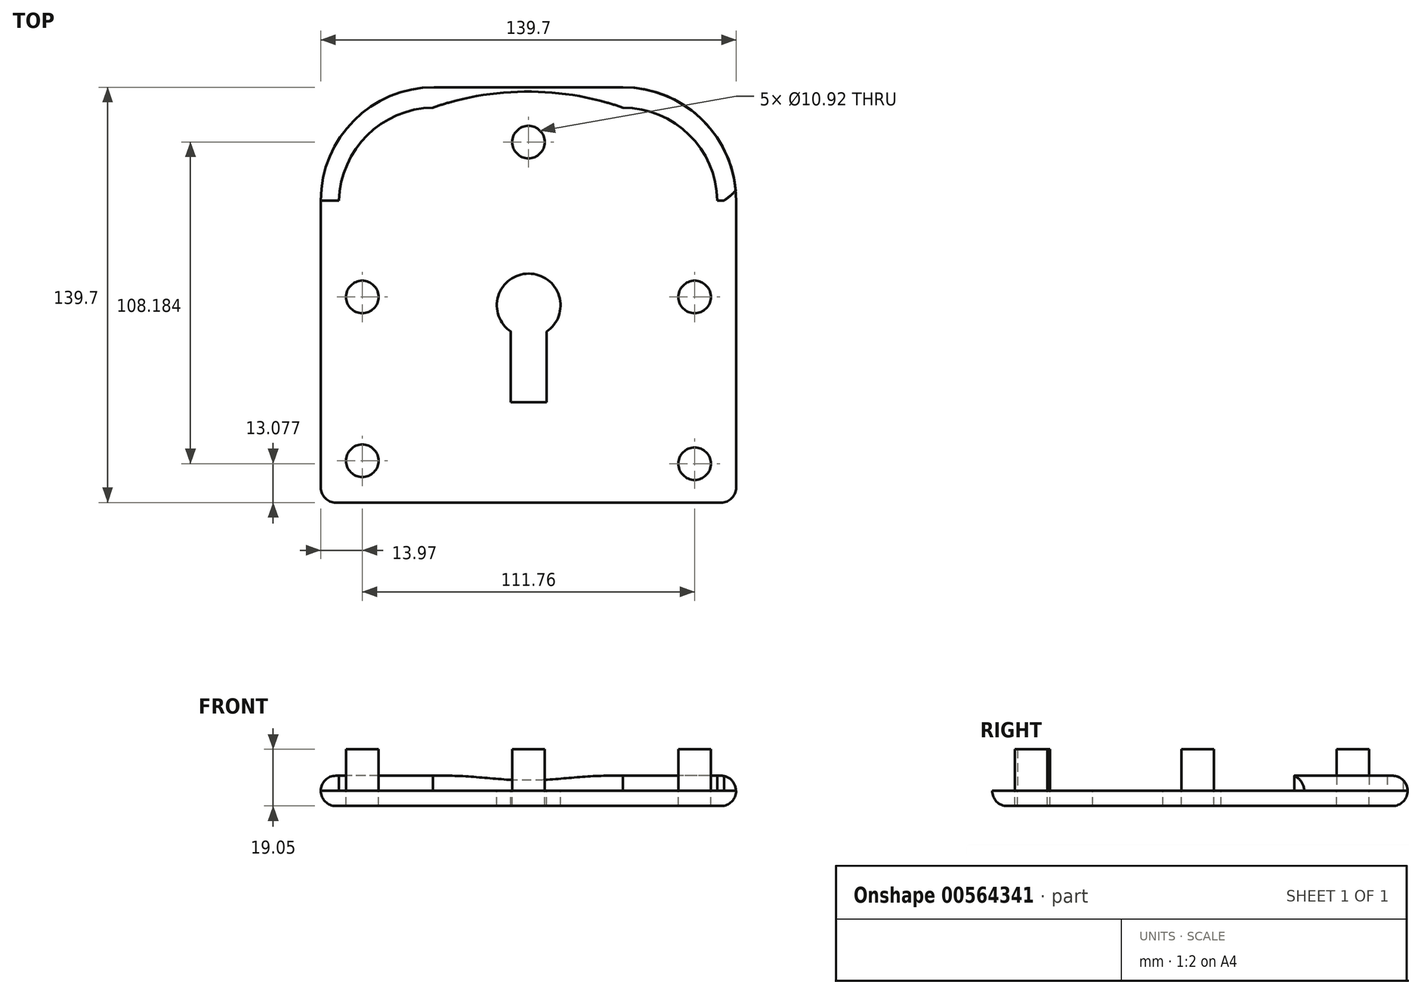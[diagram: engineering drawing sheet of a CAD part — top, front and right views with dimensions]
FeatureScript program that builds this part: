
annotation { "Feature Type Name" : "Feature", "Feature Type Description" : "" }
export const myFeature = defineFeature(function(context is Context, id is Id, definition is map)
    precondition{}
    {
        {
            var Q0;
            Q0=qCreatedBy(makeId("Top.planeOp"),FACE);
            var sketch = newSketch(context, id + "F0", { "sketchPlane" : qUnion([Q0])});
            skLineSegment(sketch, "E0.bottom", {"start": v(-31.75, 79.19) * mm, "end": v(31.75, 79.19) * mm});
            skLineSegment(sketch, "E0.top", {"start": v(-69.85, -60.51) * mm, "end": v(69.85, -60.51) * mm});
            skLineSegment(sketch, "E0.left", {"start": v(-69.85, 41.09) * mm, "end": v(-69.85, -60.51) * mm});
            skLineSegment(sketch, "E0.right", {"start": v(69.85, 41.09) * mm, "end": v(69.85, -60.51) * mm});
            skPoint(sketch, "E1.0.internal.snap0", {"position": v(0, -60.51) * mm});
            skPoint(sketch, "E2.orphan", {"position": v(-69.85, 32.63) * mm});
            skPoint(sketch, "E3.1.internal.snap0", {"position": v(27.83, 44.56) * mm});
            skFitSpline(sketch, "E3", {"points": [v(27.83, 44.56) * mm, v(69.85, 44.56) * mm], "startDerivative": vector(74.5, -35.49) * mm, "endDerivative": vector(22.58, 22.62) * mm});
            skPoint(sketch, "E4.orphan", {"position": v(73.2, 110.43) * mm});
            skPoint(sketch, "E5.start.orphan", {"position": v(69.85, 41.09) * mm});
            skCircle(sketch, "E6", {"center": v(0, 60.75) * mm, "radius": 5.46 * mm});
            skCircle(sketch, "E7", {"center": v(55.88, 8.65) * mm, "radius": 5.46 * mm});
            skCircle(sketch, "E8", {"center": v(55.88, -47.43) * mm, "radius": 5.46 * mm});
            skPoint(sketch, "E9.visualSharp", {"position": v(-69.85, 79.19) * mm});
            skArc(sketch, "E9.filletArc", {"start": v(-31.75, 79.19) * mm, "mid": v(-58.7, 68.03) * mm, "end": v(-69.85, 41.09) * mm});
            skPoint(sketch, "E10.visualSharp", {"position": v(69.85, 79.19) * mm});
            skArc(sketch, "E10.filletArc", {"start": v(69.85, 41.09) * mm, "mid": v(58.7, 68.03) * mm, "end": v(31.75, 79.19) * mm});
            skCircle(sketch, "E11", {"center": v(-55.88, 8.65) * mm, "radius": 5.46 * mm});
            skCircle(sketch, "E12", {"center": v(-55.88, -46.46) * mm, "radius": 5.46 * mm});
            skPoint(sketch, "E13.start.orphan", {"position": v(0, 79.19) * mm});
            skPoint(sketch, "E14.end.orphan", {"position": v(0, 74.72) * mm});
            skPoint(sketch, "E15.start.orphan", {"position": v(-64.1, 32.63) * mm});
            skPoint(sketch, "E16.end.orphan", {"position": v(-58.36, 32.63) * mm});
            skPoint(sketch, "E17.end.orphan", {"position": v(128.83, 32.86) * mm});
            skPoint(sketch, "E18.end.orphan", {"position": v(41.2, 32.63) * mm});
            skPoint(sketch, "E19.right.end.orphan", {"position": v(-17.52, -21.31) * mm});
            skPoint(sketch, "E20.left.start.orphan", {"position": v(48.52, 32.63) * mm});
            skPoint(sketch, "E21.top.end.orphan", {"position": v(10.9, -44.82) * mm});
            skPoint(sketch, "E22.start.orphan", {"position": v(0, -44.82) * mm});
            skPoint(sketch, "E23.bottom.start.orphan", {"position": v(44.9, 0) * mm});
            skPoint(sketch, "E24.bottom.start.orphan", {"position": v(-62.6, 0) * mm});
            skLineSegment(sketch, "E25", {"start": v(-69.85, 41.09) * mm, "end": v(-63.7, 41.09) * mm});
            skLineSegment(sketch, "E26.bottom", {"start": v(-5.9, -3.04) * mm, "end": v(-5.91, -3.04) * mm});
            skLineSegment(sketch, "E26.top", {"start": v(6.06, -26.7) * mm, "end": v(-5.91, -26.7) * mm});
            skLineSegment(sketch, "E26.left", {"start": v(6.06, -3.04) * mm, "end": v(6.06, -26.7) * mm});
            skLineSegment(sketch, "E26.right", {"start": v(-5.91, -3.04) * mm, "end": v(-5.91, -26.7) * mm});
            skArc(sketch, "E27", {"start": v(-32.19, 72.34) * mm, "mid": v(-54.23, 63.06) * mm, "end": v(-63.7, 41.09) * mm});
            skArc(sketch, "E28", {"start": v(63.5, 41.09) * mm, "mid": v(54.03, 63.22) * mm, "end": v(31.75, 72.34) * mm});
            skArc(sketch, "E29", {"start": v(31.75, 72.34) * mm, "mid": v(-0.22, 77.75) * mm, "end": v(-32.19, 72.34) * mm});
            skLineSegment(sketch, "E30.trimOffspring", {"start": v(63.5, 41.09) * mm, "end": v(72.43, 41.09) * mm});
            skArc(sketch, "E31", {"start": v(6.06, -3.04) * mm, "mid": v(0.08, 16.52) * mm, "end": v(-5.9, -3.04) * mm});
            skSolve(sketch);
        }
        {
            var Q0;
            Q0=makeQuery(id+"F0.imprint","IMPRINT",FACE,{"disambiguationData":[TD([[makeQuery(id+"F0.imprint","IMPRINT",EDGE,{"derivedFrom":sQuery(id+"F0.wireOp",EDGE,"E6")}),1.0]])]});
            var Q1;
            Q1=makeQuery(id+"F0.imprint","IMPRINT",FACE,{"disambiguationData":[TD([[makeQuery(id+"F0.imprint","IMPRINT",EDGE,{"derivedFrom":sQuery(id+"F0.wireOp",EDGE,"E7")}),1.0]])]});
            var Q2;
            Q2=makeQuery(id+"F0.imprint","IMPRINT",FACE,{"disambiguationData":[TD([[makeQuery(id+"F0.imprint","IMPRINT",EDGE,{"derivedFrom":sQuery(id+"F0.wireOp",EDGE,"E8")}),1.0]])]});
            var Q3;
            Q3=makeQuery(id+"F0.imprint","IMPRINT",FACE,{"disambiguationData":[TD([[makeQuery(id+"F0.imprint","IMPRINT",EDGE,{"derivedFrom":sQuery(id+"F0.wireOp",EDGE,"E12")}),1.0]])]});
            var Q4;
            Q4=makeQuery(id+"F0.imprint","IMPRINT",FACE,{"disambiguationData":[TD([[makeQuery(id+"F0.imprint","IMPRINT",EDGE,{"derivedFrom":sQuery(id+"F0.wireOp",EDGE,"E11")}),1.0]])]});
            extrude(context, id + "F1", {"entities" : qUnion([Q0, Q1, Q2, Q3, Q4]), "depth" : 13.97 * mm, "offsetDistance" : 25.4 * mm});
        }
        {
            var Q0;
            Q0=makeQuery(id+"F1.opExtrude","CAP_FACE",FACE,{"disambiguationData":[OSD([sQuery(id+"F0.wireOp",EDGE,"E12")])],"isStart":true});
            var Q1;
            Q1=makeQuery(id+"F1.opExtrude","CAP_FACE",FACE,{"disambiguationData":[OSD([sQuery(id+"F0.wireOp",EDGE,"E7")])],"isStart":true});
            var Q2;
            Q2=makeQuery(id+"F1.opExtrude","CAP_FACE",FACE,{"disambiguationData":[OSD([sQuery(id+"F0.wireOp",EDGE,"E8")])],"isStart":true});
            var Q3;
            Q3=makeQuery(id+"F1.opExtrude","CAP_FACE",FACE,{"disambiguationData":[OSD([sQuery(id+"F0.wireOp",EDGE,"E11")])],"isStart":true});
            var Q4;
            Q4=makeQuery(id+"F1.opExtrude","CAP_FACE",FACE,{"disambiguationData":[OSD([sQuery(id+"F0.wireOp",EDGE,"E6")])],"isStart":true});
            var Q5;
            Q5 = qSketchRegion(id + "F0", true);
            extrude(context, id + "F2", {"entities" : qUnion([Q0, Q1, Q2, Q3, Q4, Q5]), "depth" : 5.08 * mm, "offsetDistance" : 25.4 * mm});
        }
        {
            var Q0;
            {var subQ5=sQuery(id+"F0.wireOp",EDGE,"E0.bottom");Q0=makeQuery(id+"F0.imprint","IMPRINT",FACE,{"disambiguationData":[TD([[makeQuery(id+"F0.imprint","IMPRINT",EDGE,{"derivedFrom":subQ5}),-1.0]])]});}
            extrude(context, id + "F3", {"entities" : qUnion([Q0]), "depth" : 5.08 * mm, "offsetDistance" : 25.4 * mm});
        }
        {
            var Q0;
            Q0=makeQuery(id+"F3.opExtrude","CAP_EDGE",EDGE,{"disambiguationData":[OSD([sQuery(id+"F0.wireOp",EDGE,"E10.filletArc")])],"isStart":false});
            var Q1;
            Q1=makeQuery(id+"F2.opExtrude","SWEPT_EDGE",EDGE,{"disambiguationData":[OSD([sQuery(id+"F0.wireOp",EDGE,"E0.top"),sQuery(id+"F0.wireOp",EDGE,"E0.right")])]});
            var Q2;
            Q2=makeQuery(id+"F2.opExtrude","SWEPT_EDGE",EDGE,{"disambiguationData":[OSD([sQuery(id+"F0.wireOp",EDGE,"E0.top"),sQuery(id+"F0.wireOp",EDGE,"E0.left")])]});
            var Q3;
            Q3=makeQuery(id+"F2.opExtrude","CAP_EDGE",EDGE,{"disambiguationData":[OSD([sQuery(id+"F0.wireOp",EDGE,"E0.top")])],"isStart":false});
            var Q4;
            Q4=makeQuery(id+"F2.opExtrude","CAP_EDGE",EDGE,{"disambiguationData":[OSD([sQuery(id+"F0.wireOp",EDGE,"E10.filletArc")])],"isStart":false});
            fillet(context, id + "F4", {"entities" : qUnion([Q0, Q1, Q2, Q3, Q4]), "radius" : 5.08 * mm, "tangentPropagation" : true, "allowEdgeOverflow" : false});
        }
    });
